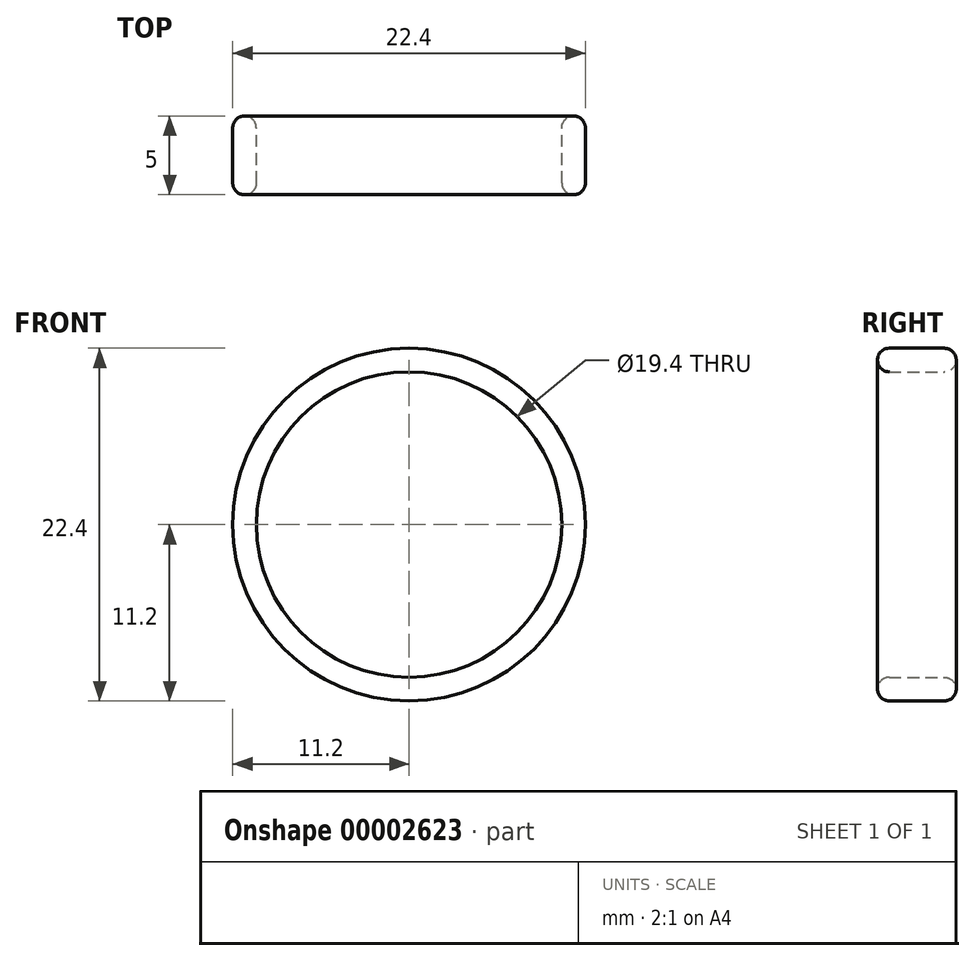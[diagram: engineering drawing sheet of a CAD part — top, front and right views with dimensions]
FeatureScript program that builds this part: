
annotation { "Feature Type Name" : "Feature", "Feature Type Description" : "" }
export const myFeature = defineFeature(function(context is Context, id is Id, definition is map)
    precondition{}
    {
        {
            var Q0;
            Q0=qCreatedBy(makeId("Right.planeOp"),FACE);
            var sketch = newSketch(context, id + "F0", { "sketchPlane" : qUnion([Q0])});
            skLineSegment(sketch, "E0", {"start": v(-2.5, 9.7) * mm, "end": v(2.5, 9.7) * mm, "construction": true});
            skLineSegment(sketch, "E1", {"start": v(2.5, 9.7) * mm, "end": v(2.5, 0) * mm, "construction": true});
            skLineSegment(sketch, "E2", {"start": v(2.5, 0) * mm, "end": v(-1.31, 0) * mm});
            skLineSegment(sketch, "E3.rect.bottom", {"start": v(1.75, 9.7) * mm, "end": v(-1.75, 9.7) * mm});
            skLineSegment(sketch, "E3.rect.top", {"start": v(1.75, 11.2) * mm, "end": v(-1.75, 11.2) * mm});
            skLineSegment(sketch, "E3.rect.left", {"start": v(2.5, 10.45) * mm, "end": v(2.5, 10.45) * mm});
            skLineSegment(sketch, "E3.rect.right", {"start": v(-2.5, 10.45) * mm, "end": v(-2.5, 10.45) * mm});
            skPoint(sketch, "E3.rect.middle", {"position": v(0, 10.45) * mm});
            skPoint(sketch, "E4.visualSharp", {"position": v(2.5, 11.2) * mm});
            skArc(sketch, "E4.filletArc", {"start": v(2.5, 10.45) * mm, "mid": v(2.28, 10.98) * mm, "end": v(1.75, 11.2) * mm});
            skPoint(sketch, "E5.visualSharp", {"position": v(2.5, 9.7) * mm});
            skArc(sketch, "E5.filletArc", {"start": v(1.75, 9.7) * mm, "mid": v(2.28, 9.92) * mm, "end": v(2.5, 10.45) * mm});
            skPoint(sketch, "E6.visualSharp", {"position": v(-2.5, 9.7) * mm});
            skArc(sketch, "E6.filletArc", {"start": v(-2.5, 10.45) * mm, "mid": v(-2.28, 9.92) * mm, "end": v(-1.75, 9.7) * mm});
            skPoint(sketch, "E7.visualSharp", {"position": v(-2.5, 11.2) * mm});
            skArc(sketch, "E7.filletArc", {"start": v(-1.75, 11.2) * mm, "mid": v(-2.28, 10.98) * mm, "end": v(-2.5, 10.45) * mm});
            skSolve(sketch);
        }
        {
            var Q0;
            Q0=makeQuery(id+"F0.imprint","IMPRINT",FACE,{"disambiguationData":[TD([[makeQuery(id+"F0.imprint","IMPRINT",EDGE,{"derivedFrom":sQuery(id+"F0.wireOp",EDGE,"E3.rect.bottom")}),-1.0]])]});
            var Q1;
            Q1=sQuery(id+"F0.wireOp",EDGE,"E2");
            revolve(context, id + "F1", {"entities" : qUnion([Q0]), "axis" : qUnion([Q1]), "revolveType" : RevolveType.FULL});
        }
    });
